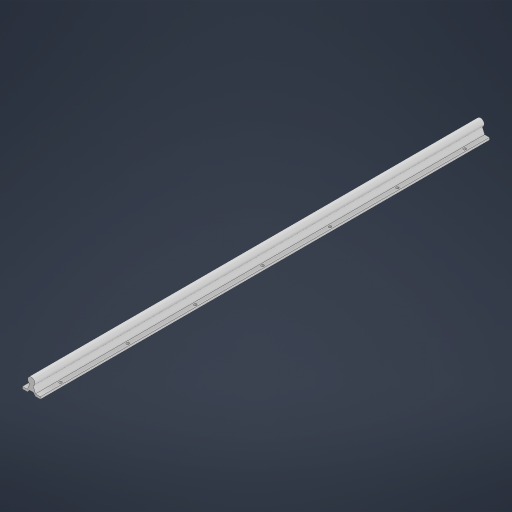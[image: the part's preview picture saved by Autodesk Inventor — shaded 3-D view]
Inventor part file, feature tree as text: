
AUTODESK INVENTOR PART (.ipt)
format: ipt  version: 2024 (Build 280153000, 153)  size: 226,304 bytes
history: native  units: mm
features: extrude x2, sketch x2, pattern_linear x1, mirror x1
ambient origin geometry x8: Origin, YZ Plane, XZ Plane, XY Plane, X Axis, Y Axis, Z Axis, Center Point
bodies: Solid1 (feature_tree)
feature tree (6):
  extrude  "Extrusion1"  Depth=39.8mm
  extrude  "Extrusion2"  Depth=1000.0mm
  pattern_linear  "Rectangular Pattern1"  Spacing1=32.7mm  [1 undecoded]
  mirror  "Mirror1"
  sketch  "Sketch1"  dims[d0=16.0mm d1=39.8mm]
  sketch  "Sketch2"  dims[d2=5.0mm d4=10.8mm d7=32.7mm d8=7.7mm d9=9.0mm d10=5.6mm d11=17.7mm d12=1000.0mm d13=0.0mm d14=50.0mm d15=6.0mm d16=0.0mm d17=0.0mm d18=70.0mm d20=150.0mm]
note: 1 required parameter value undecoded (feature->parameter linkage not recoverable at this tier; creation-order binding heuristic only, values carry confidence <= 0.55)
